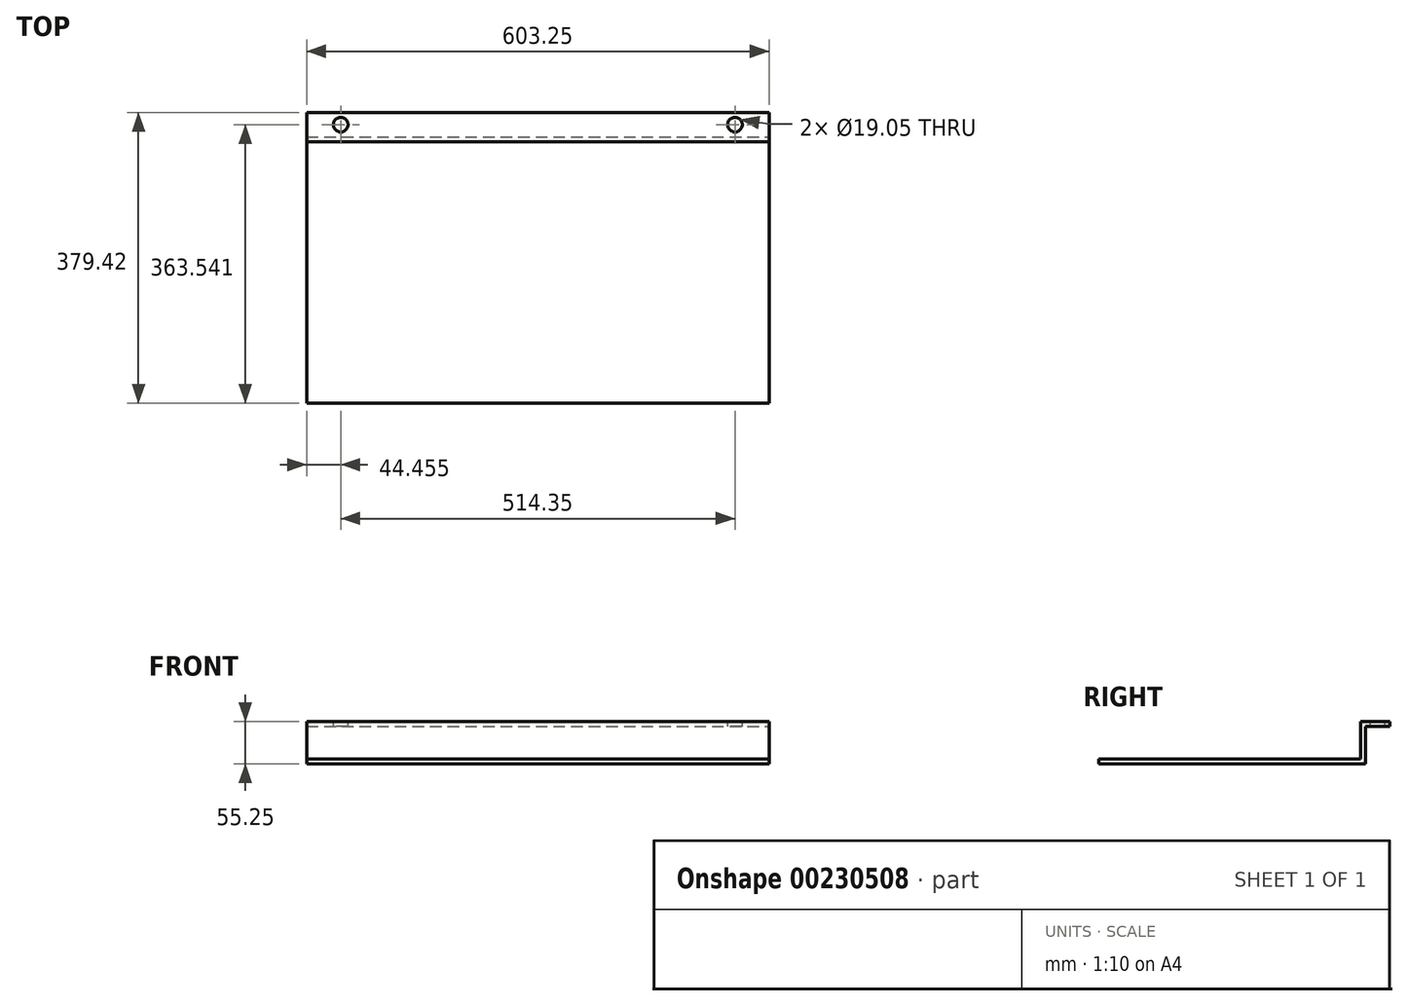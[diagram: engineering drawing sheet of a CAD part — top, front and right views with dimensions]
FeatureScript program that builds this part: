
annotation { "Feature Type Name" : "Feature", "Feature Type Description" : "" }
export const myFeature = defineFeature(function(context is Context, id is Id, definition is map)
    precondition{}
    {
        {
            var Q0;
            Q0=qCreatedBy(makeId("Top.planeOp"),FACE);
            var sketch = newSketch(context, id + "F0", { "sketchPlane" : qUnion([Q0])});
            skLineSegment(sketch, "E0.bottom", {"start": v(-309.69, 174.29) * mm, "end": v(293.56, 174.29) * mm});
            skLineSegment(sketch, "E0.top", {"start": v(-309.69, -173.38) * mm, "end": v(293.56, -173.38) * mm});
            skLineSegment(sketch, "E0.left", {"start": v(-309.69, 174.29) * mm, "end": v(-309.69, -173.38) * mm});
            skLineSegment(sketch, "E0.right", {"start": v(293.56, 174.29) * mm, "end": v(293.56, -173.38) * mm});
            skSolve(sketch);
        }
        {
            var Q0;
            Q0 = qSketchRegion(id + "F0", true);
            extrude(context, id + "F1", {"entities" : qUnion([Q0]), "depth" : 6.35 * mm});
        }
        {
            var Q0;
            Q0=makeQuery(id+"F1.opExtrude","CAP_FACE",FACE,{"disambiguationData":[OSD([sQuery(id+"F0.wireOp",EDGE,"E0.bottom"),sQuery(id+"F0.wireOp",EDGE,"E0.top"),sQuery(id+"F0.wireOp",EDGE,"E0.left"),sQuery(id+"F0.wireOp",EDGE,"E0.right")])],"isStart":false});
            var sketch = newSketch(context, id + "F2", { "sketchPlane" : qUnion([Q0])});
            skLineSegment(sketch, "E1.bottom", {"start": v(-309.69, 174.29) * mm, "end": v(293.56, 174.29) * mm});
            skLineSegment(sketch, "E1.top", {"start": v(-309.69, 167.94) * mm, "end": v(293.56, 167.94) * mm});
            skLineSegment(sketch, "E1.left", {"start": v(-309.69, 174.29) * mm, "end": v(-309.69, 167.94) * mm});
            skLineSegment(sketch, "E1.right", {"start": v(293.56, 174.29) * mm, "end": v(293.56, 167.94) * mm});
            skSolve(sketch);
        }
        {
            var Q0;
            Q0 = qSketchRegion(id + "F2", true);
            extrude(context, id + "F3", {"entities" : qUnion([Q0]), "operationType" : NewBodyOperationType.ADD, "depth" : 42.55 * mm});
        }
        {
            var Q0;
            Q0=makeQuery(id+"F3.opExtrude","CAP_FACE",FACE,{"disambiguationData":[OSD([sQuery(id+"F2.wireOp",EDGE,"E1.bottom"),sQuery(id+"F2.wireOp",EDGE,"E1.top"),sQuery(id+"F2.wireOp",EDGE,"E1.left"),sQuery(id+"F2.wireOp",EDGE,"E1.right")])],"isStart":false});
            var sketch = newSketch(context, id + "F4", { "sketchPlane" : qUnion([Q0])});
            skLineSegment(sketch, "E2.bottom", {"start": v(-309.69, 167.94) * mm, "end": v(293.56, 167.94) * mm});
            skLineSegment(sketch, "E2.top", {"start": v(-309.69, 206.04) * mm, "end": v(293.56, 206.04) * mm});
            skLineSegment(sketch, "E2.left", {"start": v(-309.69, 167.94) * mm, "end": v(-309.69, 206.04) * mm});
            skLineSegment(sketch, "E2.right", {"start": v(293.56, 167.94) * mm, "end": v(293.56, 206.04) * mm});
            skSolve(sketch);
        }
        {
            var Q0;
            Q0 = qSketchRegion(id + "F4", true);
            extrude(context, id + "F5", {"entities" : qUnion([Q0]), "operationType" : NewBodyOperationType.ADD, "depth" : 6.35 * mm});
        }
        {
            var Q0;
            Q0=makeQuery(id+"F5.opExtrude","CAP_FACE",FACE,{"disambiguationData":[OSD([sQuery(id+"F4.wireOp",EDGE,"E2.bottom"),sQuery(id+"F4.wireOp",EDGE,"E2.top"),sQuery(id+"F4.wireOp",EDGE,"E2.left"),sQuery(id+"F4.wireOp",EDGE,"E2.right")])],"isStart":false});
            var sketch = newSketch(context, id + "F6", { "sketchPlane" : qUnion([Q0])});
            skCircle(sketch, "E3", {"center": v(-265.24, 190.16) * mm, "radius": 9.53 * mm});
            skPoint(sketch, "E3.centerSnap0", {"position": v(-309.69, 190.16) * mm});
            skCircle(sketch, "E4", {"center": v(249.11, 190.16) * mm, "radius": 9.53 * mm});
            skPoint(sketch, "E4.centerSnap0", {"position": v(293.56, 190.16) * mm});
            skSolve(sketch);
        }
        {
            var Q0;
            Q0 = qSketchRegion(id + "F6", true);
            extrude(context, id + "F7", {"entities" : qUnion([Q0]), "operationType" : NewBodyOperationType.REMOVE, "endBound" : BoundingType.THROUGH_ALL, "oppositeDirection" : true, "depth" : 25.4 * mm});
        }
    });
